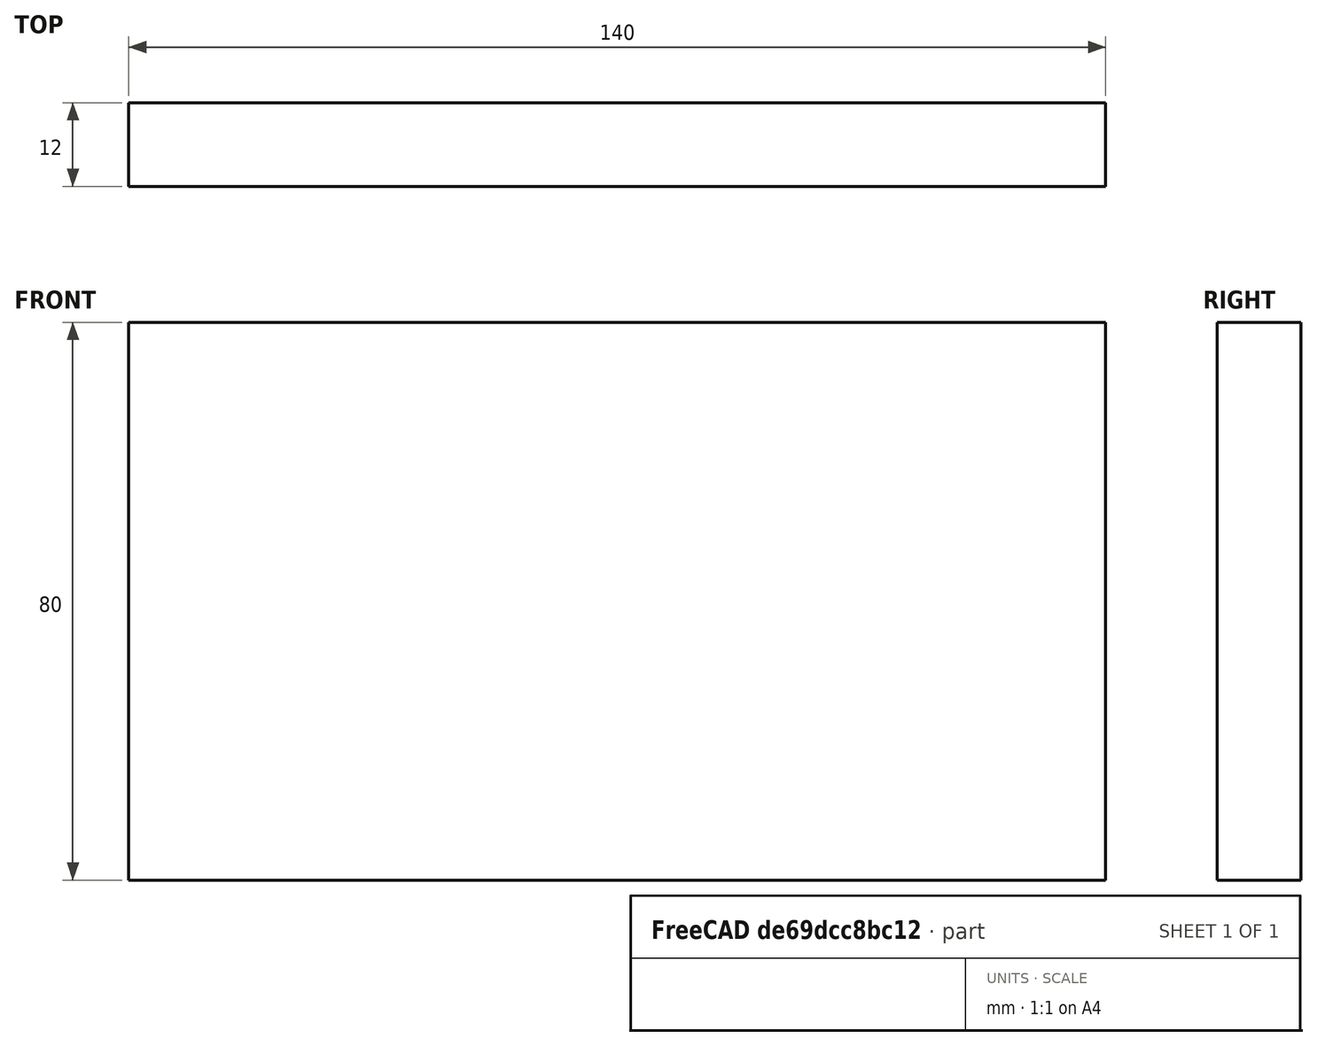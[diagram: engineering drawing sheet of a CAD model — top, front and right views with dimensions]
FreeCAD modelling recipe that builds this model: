
FCSTD DOCUMENT  (FreeCAD 0.20R29177 (Git))
Label: 1001_keyboard_sidewall_12_
License: All rights reserved
LicenseURL: http://en.wikipedia.org/wiki/All_rights_reserved
objects: Sketcher::SketchObject×1, PartDesign::Pad×1, PartDesign::Body×1, Spreadsheet::Sheet×1
note: 4 computed .brp shape members not serialized (recipe doc carries the construction recipe); baked Part::Feature solids carry a one-line shape summary decoded from their .brp

FEATURE [Sketcher::SketchObject] Sketch  label="SideWall"
  FullyConstrained = true
  MapMode = 5
  Placement = pos=(0,0,0) rot=(1,0,0;1.5708rad)
  Support = -> [XZ_Plane]
  expr: .Constraints.z_0 = <<xls>>.z_0
  expr: Constraints[10] = <<xls>>.X0
  sketch-geometry (4):
    g0: LineSegment StartX=140 StartY=0 StartZ=0 EndX=0 EndY=0 EndZ=0
    g1: LineSegment StartX=0 StartY=0 StartZ=0 EndX=0 EndY=80 EndZ=0
    g2: LineSegment StartX=0 StartY=80 StartZ=0 EndX=140 EndY=80 EndZ=0
    g3: LineSegment StartX=140 StartY=80 StartZ=0 EndX=140 EndY=0 EndZ=0
  constraints (11):
    c: Coincident(g0,g-1)
    c: Horizontal(g0)
    c: Coincident(g1,g-1)
    c: Vertical(g1)
    c: Coincident(g2,g1)
    c: Vertical(g3)
    c: Coincident(g0,g3)
    c: Perpendicular(g1,g2)
    c: DistanceY(g1,g1) = 80  'z_0'
    c: Coincident(g3,g2)
    c: DistanceX(g2,g2) = 140
FEATURE [PartDesign::Pad] Pad
  AllowMultiFace = false
  Direction = (0,-1,-1.035e-13)
  Length = 12
  Length2 = 13
  Placement = pos=(0,0,0) rot=(1,0,0;1.5708rad)
  Profile = -> Sketch
  ReferenceAxis = -> Sketch [N_Axis]
  Reversed = true
  Type = 0
FEATURE [PartDesign::Body] Body
  Group = -> [Sketch,Pad]
  Origin = -> Origin
  Tip = -> Pad
FEATURE [Spreadsheet::Sheet] Spreadsheet  label="xls"
  cells = C2=INHERITED DIMENSIONS; C3=Thickness; D3=kbf_t_0; E3=16; F3=mm; H3=NOTE: No plexi; C5=SIDEWALL ; C6=thickness of board; D6=t; E6(nt)=12; F6=mm; C7=Depth of Board; E7=150; G7=NOMINAL; C8=Depth of board; D8=X0; E8(X0)=140; F8=mm; G8=REAL; C9=Height of board; D9=Z0; E9(z_0)=80; F9=mm
